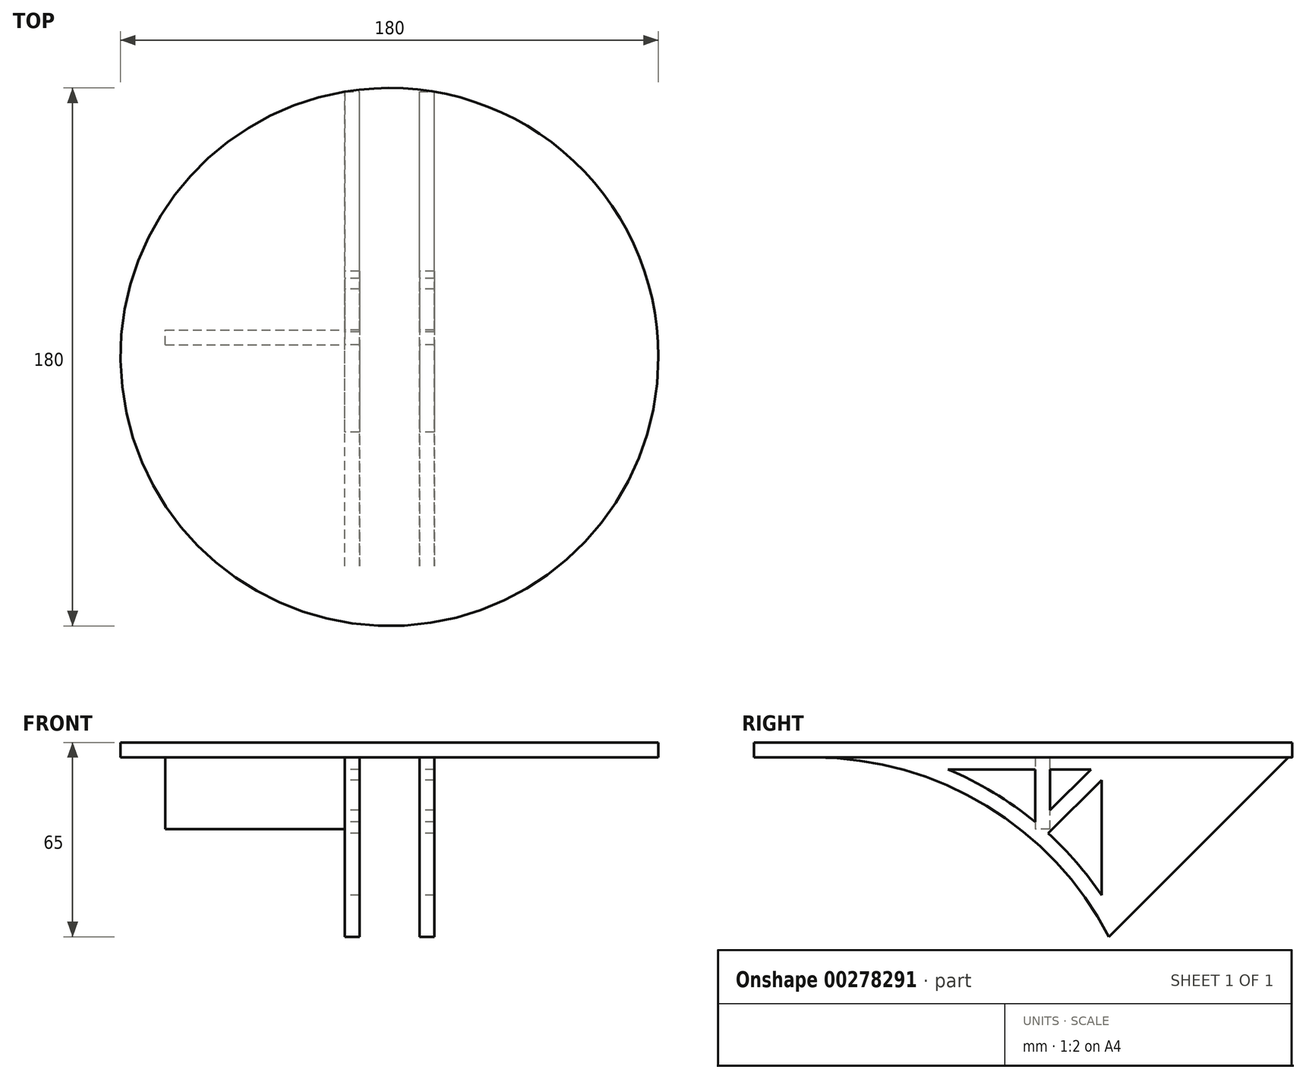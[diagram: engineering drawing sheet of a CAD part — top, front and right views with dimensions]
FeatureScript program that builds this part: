
annotation { "Feature Type Name" : "Feature", "Feature Type Description" : "" }
export const myFeature = defineFeature(function(context is Context, id is Id, definition is map)
    precondition{}
    {
        {
            var Q0;
            Q0=qCreatedBy(makeId("Top.planeOp"),FACE);
            var sketch = newSketch(context, id + "F0", { "sketchPlane" : qUnion([Q0])});
            skCircle(sketch, "E0", {"center": v(0, 0) * mm, "radius": 90 * mm});
            skSolve(sketch);
        }
        {
            var Q0;
            Q0 = qSketchRegion(id + "F0", true);
            extrude(context, id + "F1", {"entities" : qUnion([Q0]), "depth" : 5 * mm});
        }
        {
            var Q0;
            Q0=makeQuery(id+"F1.opExtrude","CAP_FACE",FACE,{"disambiguationData":[OSD([sQuery(id+"F0.wireOp",EDGE,"E0")])],"isStart":true});
            var sketch = newSketch(context, id + "F2", { "sketchPlane" : qUnion([Q0])});
            skLineSegment(sketch, "E1.bottom", {"start": v(-15, 70) * mm, "end": v(-10, 70) * mm});
            skLineSegment(sketch, "E1.top", {"start": v(-15, -88.74) * mm, "end": v(-10, -88.74) * mm});
            skLineSegment(sketch, "E1.left", {"start": v(-15, 70) * mm, "end": v(-15, -88.74) * mm});
            skLineSegment(sketch, "E1.right", {"start": v(15, 70) * mm, "end": v(15, -88.74) * mm});
            skLineSegment(sketch, "E2", {"start": v(-10, 70) * mm, "end": v(-10, -88.74) * mm});
            skLineSegment(sketch, "E3", {"start": v(10, 70) * mm, "end": v(10, -88.74) * mm});
            skLineSegment(sketch, "E4.trimOffspring", {"start": v(10, 70) * mm, "end": v(15, 70) * mm});
            skLineSegment(sketch, "E5.trimOffspring", {"start": v(10, -88.74) * mm, "end": v(15, -88.74) * mm});
            skSolve(sketch);
        }
        {
            var Q0;
            Q0 = qSketchRegion(id + "F2", true);
            extrude(context, id + "F3", {"entities" : qUnion([Q0]), "operationType" : NewBodyOperationType.ADD, "depth" : 60 * mm});
        }
        {
            var Q0;
            Q0=makeQuery(id+"F3.opExtrude","SWEPT_FACE",FACE,{"disambiguationData":[OSD([sQuery(id+"F2.wireOp",EDGE,"E1.left")])]});
            var sketch = newSketch(context, id + "F4", { "sketchPlane" : qUnion([Q0])});
            skLineSegment(sketch, "E6", {"start": v(-88.74, 0) * mm, "end": v(-28.74, -60) * mm});
            skArc(sketch, "E7", {"start": v(70, 0) * mm, "mid": v(12.23, -16.18) * mm, "end": v(-28.74, -60) * mm});
            skLineSegment(sketch, "E8", {"start": v(-28.74, -60) * mm, "end": v(-28.74, 0) * mm, "construction": true});
            skLineSegment(sketch, "E9", {"start": v(-22.7, -4) * mm, "end": v(-9.01, -4) * mm});
            skLineSegment(sketch, "E10", {"start": v(25.15, -4) * mm, "end": v(-4.01, -4) * mm});
            skLineSegment(sketch, "E11", {"start": v(-26.24, -7.54) * mm, "end": v(-26.24, -46.05) * mm});
            skArc(sketch, "E12", {"start": v(25.15, -4) * mm, "mid": v(9.92, -11.73) * mm, "end": v(-4.01, -21.6) * mm});
            skLineSegment(sketch, "E13", {"start": v(-26.24, -4) * mm, "end": v(-6.51, -23.73) * mm, "construction": true});
            skLineSegment(sketch, "E14", {"start": v(-26.24, -7.54) * mm, "end": v(-8.38, -25.4) * mm});
            skLineSegment(sketch, "E15", {"start": v(-22.7, -4) * mm, "end": v(-9.01, -17.7) * mm});
            skArc(sketch, "E16.trimOffspring", {"start": v(-8.38, -25.4) * mm, "mid": v(-17.92, -35.2) * mm, "end": v(-26.24, -46.05) * mm});
            skLineSegment(sketch, "E17", {"start": v(-88.74, 0) * mm, "end": v(-88.74, -60) * mm});
            skLineSegment(sketch, "E18", {"start": v(-88.74, -60) * mm, "end": v(-28.74, -60) * mm});
            skLineSegment(sketch, "E19", {"start": v(-28.74, -60) * mm, "end": v(70, -60) * mm});
            skLineSegment(sketch, "E20", {"start": v(70, -60) * mm, "end": v(70, 0) * mm});
            skLineSegment(sketch, "E21", {"start": v(-6.51, -23.73) * mm, "end": v(-6.51, 0) * mm, "construction": true});
            skLineSegment(sketch, "E22", {"start": v(-9.01, -4) * mm, "end": v(-9.01, -17.7) * mm});
            skLineSegment(sketch, "E23", {"start": v(-4.01, -4) * mm, "end": v(-4.01, -21.6) * mm});
            skLineSegment(sketch, "E24.trimOffspring", {"start": v(-9.01, -4) * mm, "end": v(-22.7, -4) * mm});
            skLineSegment(sketch, "E25.trimOffspring", {"start": v(-4.01, -4) * mm, "end": v(25.15, -4) * mm});
            skSolve(sketch);
        }
        {
            var Q0;
            Q0 = qSketchRegion(id + "F4", true);
            extrude(context, id + "F5", {"entities" : qUnion([Q0]), "operationType" : NewBodyOperationType.REMOVE, "endBound" : BoundingType.THROUGH_ALL, "oppositeDirection" : true, "depth" : 25 * mm});
        }
        {
            var Q0;
            Q0=makeQuery(id+"F3.opExtrude","SWEPT_FACE",FACE,{"disambiguationData":[OSD([sQuery(id+"F2.wireOp",EDGE,"E1.left")])]});
            var sketch = newSketch(context, id + "F6", { "sketchPlane" : qUnion([Q0])});
            skLineSegment(sketch, "E26.top", {"start": v(-9.01, -24) * mm, "end": v(-4.01, -24) * mm});
            skLineSegment(sketch, "E26.right", {"start": v(-4.01, 0) * mm, "end": v(-4.01, -24) * mm});
            skLineSegment(sketch, "E27", {"start": v(-9.01, -24) * mm, "end": v(-9.01, 0) * mm});
            skLineSegment(sketch, "E28", {"start": v(-4.01, 0) * mm, "end": v(-9.01, 0) * mm});
            skSolve(sketch);
        }
        {
            var Q0;
            Q0 = qSketchRegion(id + "F6", true);
            extrude(context, id + "F7", {"entities" : qUnion([Q0]), "operationType" : NewBodyOperationType.ADD, "depth" : 60 * mm});
        }
    });
